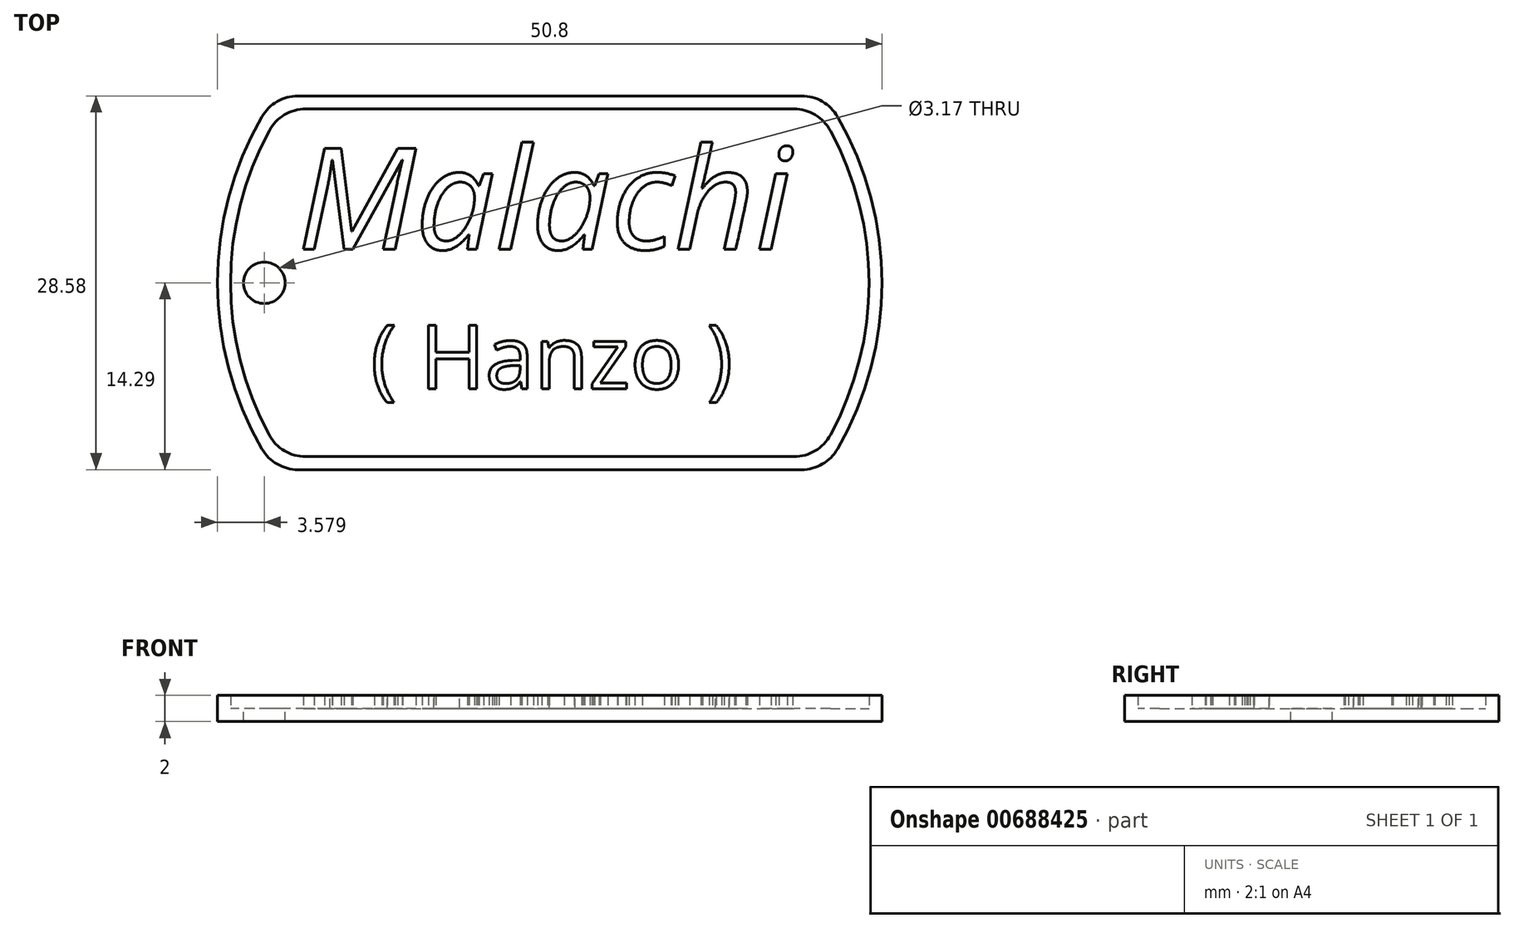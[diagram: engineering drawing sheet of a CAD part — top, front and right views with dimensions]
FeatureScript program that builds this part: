
annotation { "Feature Type Name" : "Feature", "Feature Type Description" : "" }
export const myFeature = defineFeature(function(context is Context, id is Id, definition is map)
    precondition{}
    {
        {
            var Q0;
            Q0=qCreatedBy(makeId("Top.planeOp"),FACE);
            var sketch = newSketch(context, id + "F0", { "sketchPlane" : qUnion([Q0])});
            skArc(sketch, "E0", {"start": v(-22, 12.7) * mm, "mid": v(-25.4, 0) * mm, "end": v(-22, -12.7) * mm});
            skLineSegment(sketch, "E1.top", {"start": v(-19.25, -14.29) * mm, "end": v(19.25, -14.29) * mm});
            skArc(sketch, "E2.trimOffspring", {"start": v(22, -12.7) * mm, "mid": v(25.4, 0) * mm, "end": v(22, 12.7) * mm});
            skLineSegment(sketch, "E3", {"start": v(-19.25, 14.29) * mm, "end": v(19.25, 14.29) * mm});
            skPoint(sketch, "E4.visualSharp", {"position": v(-21, 14.29) * mm});
            skArc(sketch, "E4.filletArc", {"start": v(-19.25, 14.29) * mm, "mid": v(-20.83, 13.86) * mm, "end": v(-22, 12.7) * mm});
            skPoint(sketch, "E5.visualSharp", {"position": v(21, 14.29) * mm});
            skArc(sketch, "E5.filletArc", {"start": v(22, 12.7) * mm, "mid": v(20.83, 13.86) * mm, "end": v(19.25, 14.29) * mm});
            skPoint(sketch, "E6.visualSharp", {"position": v(21, -14.29) * mm});
            skArc(sketch, "E6.filletArc", {"start": v(19.25, -14.29) * mm, "mid": v(20.83, -13.86) * mm, "end": v(22, -12.7) * mm});
            skPoint(sketch, "E7.visualSharp", {"position": v(-21, -14.29) * mm});
            skArc(sketch, "E7.filletArc", {"start": v(-22, -12.7) * mm, "mid": v(-20.83, -13.86) * mm, "end": v(-19.25, -14.29) * mm});
            skSolve(sketch);
        }
        {
            var Q0;
            Q0=makeQuery(id+"F0.imprint","IMPRINT",FACE,{"disambiguationData":[TD([[makeQuery(id+"F0.imprint","IMPRINT",EDGE,{"derivedFrom":sQuery(id+"F0.wireOp",EDGE,"E0")}),1.0]])]});
            extrude(context, id + "F1", {"entities" : qUnion([Q0]), "depth" : 1 * mm, "offsetDistance" : 25.4 * mm});
        }
        {
            var Q0;
            Q0=makeQuery(id+"F1.opExtrude","CAP_FACE",FACE,{"disambiguationData":[OSD([sQuery(id+"F0.wireOp",EDGE,"E0"),sQuery(id+"F0.wireOp",EDGE,"E1.top"),sQuery(id+"F0.wireOp",EDGE,"E2.trimOffspring"),sQuery(id+"F0.wireOp",EDGE,"E3"),sQuery(id+"F0.wireOp",EDGE,"E4.filletArc"),sQuery(id+"F0.wireOp",EDGE,"E5.filletArc"),sQuery(id+"F0.wireOp",EDGE,"E6.filletArc"),sQuery(id+"F0.wireOp",EDGE,"E7.filletArc")])],"isStart":false});
            var sketch = newSketch(context, id + "F2", { "sketchPlane" : qUnion([Q0])});
            skLineSegment(sketch, "E8.0", {"start": v(-18.66, 13.29) * mm, "end": v(18.66, 13.29) * mm});
            skArc(sketch, "E8.1", {"start": v(-21.45, 11.63) * mm, "mid": v(-24.4, 0) * mm, "end": v(-21.45, -11.63) * mm});
            skLineSegment(sketch, "E8.2", {"start": v(-18.66, -13.29) * mm, "end": v(18.66, -13.29) * mm});
            skArc(sketch, "E8.3", {"start": v(21.45, -11.63) * mm, "mid": v(24.4, 0) * mm, "end": v(21.45, 11.63) * mm});
            skPoint(sketch, "E9.visualSharp", {"position": v(-20.46, 13.29) * mm});
            skArc(sketch, "E9.filletArc", {"start": v(-18.66, 13.29) * mm, "mid": v(-20.29, 12.84) * mm, "end": v(-21.45, 11.63) * mm});
            skPoint(sketch, "E10.visualSharp", {"position": v(20.46, 13.29) * mm});
            skArc(sketch, "E10.filletArc", {"start": v(21.45, 11.63) * mm, "mid": v(20.29, 12.84) * mm, "end": v(18.66, 13.29) * mm});
            skPoint(sketch, "E11.visualSharp", {"position": v(20.46, -13.29) * mm});
            skArc(sketch, "E11.filletArc", {"start": v(18.66, -13.29) * mm, "mid": v(20.29, -12.84) * mm, "end": v(21.45, -11.63) * mm});
            skPoint(sketch, "E12.visualSharp", {"position": v(-20.46, -13.29) * mm});
            skArc(sketch, "E12.filletArc", {"start": v(-21.45, -11.63) * mm, "mid": v(-20.29, -12.84) * mm, "end": v(-18.66, -13.29) * mm});
            skLineSegment(sketch, "E13.0", {"start": v(-19.25, 14.29) * mm, "end": v(19.25, 14.29) * mm});
            skArc(sketch, "E13.1", {"start": v(-22, 12.7) * mm, "mid": v(-25.4, 0) * mm, "end": v(-22, -12.7) * mm});
            skLineSegment(sketch, "E13.2", {"start": v(-19.25, -14.29) * mm, "end": v(19.25, -14.29) * mm});
            skArc(sketch, "E13.3", {"start": v(22, -12.7) * mm, "mid": v(25.4, 0) * mm, "end": v(22, 12.7) * mm});
            skPoint(sketch, "E14.visualSharp", {"position": v(-21, -14.29) * mm});
            skArc(sketch, "E14.filletArc", {"start": v(-22, -12.7) * mm, "mid": v(-20.83, -13.86) * mm, "end": v(-19.25, -14.29) * mm});
            skPoint(sketch, "E15.visualSharp", {"position": v(21, -14.29) * mm});
            skArc(sketch, "E15.filletArc", {"start": v(19.25, -14.29) * mm, "mid": v(20.83, -13.86) * mm, "end": v(22, -12.7) * mm});
            skPoint(sketch, "E16.visualSharp", {"position": v(21, 14.29) * mm});
            skArc(sketch, "E16.filletArc", {"start": v(22, 12.7) * mm, "mid": v(20.83, 13.86) * mm, "end": v(19.25, 14.29) * mm});
            skPoint(sketch, "E17.visualSharp", {"position": v(-21, 14.29) * mm});
            skArc(sketch, "E17.filletArc", {"start": v(-19.25, 14.29) * mm, "mid": v(-20.83, 13.86) * mm, "end": v(-22, 12.7) * mm});
            skSolve(sketch);
        }
        {
            var Q0;
            Q0=makeQuery(id+"F2.imprint","IMPRINT",FACE,{"disambiguationData":[TD([[makeQuery(id+"F2.imprint","IMPRINT",EDGE,{"derivedFrom":sQuery(id+"F2.wireOp",EDGE,"E8.0")}),1.0]])]});
            extrude(context, id + "F3", {"entities" : qUnion([Q0]), "operationType" : NewBodyOperationType.ADD, "depth" : 1 * mm, "offsetDistance" : 25.4 * mm});
        }
        {
            var Q0;
            Q0=makeQuery(id+"F1.opExtrude","CAP_FACE",FACE,{"disambiguationData":[OSD([sQuery(id+"F0.wireOp",EDGE,"E0"),sQuery(id+"F0.wireOp",EDGE,"E1.top"),sQuery(id+"F0.wireOp",EDGE,"E2.trimOffspring"),sQuery(id+"F0.wireOp",EDGE,"E3"),sQuery(id+"F0.wireOp",EDGE,"E4.filletArc"),sQuery(id+"F0.wireOp",EDGE,"E5.filletArc"),sQuery(id+"F0.wireOp",EDGE,"E6.filletArc"),sQuery(id+"F0.wireOp",EDGE,"E7.filletArc")])],"isStart":false});
            var sketch = newSketch(context, id + "F4", { "sketchPlane" : qUnion([Q0])});
            skCircle(sketch, "E18", {"center": v(-21.82, 0) * mm, "radius": 1.59 * mm});
            skSolve(sketch);
        }
        {
            var Q0;
            Q0=makeQuery(id+"F4.imprint","IMPRINT",FACE,{"disambiguationData":[TD([[makeQuery(id+"F4.imprint","IMPRINT",EDGE,{"derivedFrom":sQuery(id+"F4.wireOp",EDGE,"E18")}),1.0]])]});
            extrude(context, id + "F5", {"entities" : qUnion([Q0]), "operationType" : NewBodyOperationType.REMOVE, "oppositeDirection" : true, "depth" : 1 * mm, "offsetDistance" : 25.4 * mm});
        }
        {
            var Q0;
            Q0=makeQuery(id+"F2.imprint","IMPRINT",FACE,{"disambiguationData":[TD([[makeQuery(id+"F2.imprint","IMPRINT",EDGE,{"derivedFrom":sQuery(id+"F2.wireOp",EDGE,"E8.0")}),-1.0]])]});
            var sketch = newSketch(context, id + "F6", { "sketchPlane" : qUnion([Q0])});
            skText(sketch, "E19", { "text": "Malachi", "fontName": "OpenSans-Italic.ttf"});
            skText(sketch, "E20", { "text": "( Hanzo )", "fontName": "OpenSans-Regular.ttf"});
            const initialGuessF6  = {"E19": [-0.01929, 0.00257, 1, 0, 0.00776], "E20": [-0.01369, -0.00809, 1, 0, 0.00487]};
            skSetInitialGuess(sketch, initialGuessF6);
            skSolve(sketch);
        }
        {
            var Q0;
            Q0 = qSketchRegion(id + "F6", true);
            extrude(context, id + "F7", {"entities" : qUnion([Q0]), "operationType" : NewBodyOperationType.ADD, "depth" : 1 * mm, "offsetDistance" : 25.4 * mm});
        }
    });
